# Revit family: Door_Coiling_UltiGroup_Frigo 2 Plus
name_source: partatom
category: Doors
revit_build: Autodesk Revit 2018 (Build: 20170223_1515(x64)
units: mm (PartAtom-declared; Revit-internal decimal feet)

## family parameters
Always vertical = Yes
Cut with Voids When Loaded = No
Host = Wall
OmniClass Number = 23.30.10.17.27.11
OmniClass Title = Overhead Coiling
Room Calculation Point = No
Shared = No

## types (1)
- Type 1
    AcousticRating_ANZRS = N / A
    Analytic Construction = <None>
    Control box distance = 150 mm
    Control box height = 1200 mm
    Curtain Bottom = Curtain Bottom
    Curtain open = 0 mm  [stored 0 ft]
    Description = Frigo 2 Plus Door
    DoorFrameFinish_ANZRS = Painted galvanised steel - RAL 9010 standard
    DoorFrameMaterial_ANZRS = Frame material
    DoorFrameType_ANZRS = Galvanised Steel
    DoorGlazingHeight_ANZRS = 0 mm  [stored 0 ft]
    DoorGlazingWidth_ANZRS = 0 mm  [stored 0 ft]
    DoorGrilleHeight_ANZRS = 0 mm  [stored 0 ft]
    DoorGrilleWidth_ANZRS = 0 mm  [stored 0 ft]
    DoorGrille_ANZRS = No
    DoorNumberOfPanels_ANZRS = 0
    DoorOperation_ANZRS = Large Heavy-duty mushroom head push button, Push button and Emergency stop button fitted to control box
    DoorPanelBWidth_ANZRS = 0 mm  [stored 0 ft]
    DoorPanelDepth_ANZRS = 0 mm  [stored 0 ft]
    DoorPanelFinish_ANZRS = PVC Fabric Curtain
    DoorPanelHeight_ANZRS = 0 mm  [stored 0 ft]
    DoorPanelMaterial_ANZRS = Curtain Material
    DoorPanelWidth_ANZRS = 0 mm  [stored 0 ft]
    Fax = 07 846 2467
    Function = Interior
    Headroom = 950 mm  [stored 3.1168 ft]
    Heating Kit height = 150 mm
    Heating components = No
    Height = 3500 mm  [stored 11.4829 ft]
    Hood length = 360 mm  [stored 1.1811 ft]
    InstallationGroup_ANZRS = 0
    Manufacturer = Ulti Group Ltd.
    Model = Ulti Frigo 2 Plus Door
    ModifiedIssue_ANZRS = 0 $
    Send Message = http://ultigroup.co.nz
    URL = www.ultigroup.co.nz
    Wall Closure = By host
    Width = 4000 mm  [stored 13.1234 ft]

note: [stored X ft] marks values corroborated as IEEE doubles in the binary element streams (Revit-internal decimal feet)

## geometry (parser evidence)
native form markers: Sweep x19
no freeform markers — native parametric forms only
